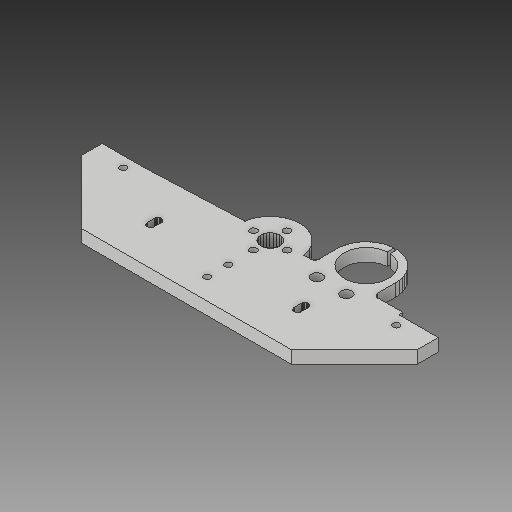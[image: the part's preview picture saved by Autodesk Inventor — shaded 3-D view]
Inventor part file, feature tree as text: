
AUTODESK INVENTOR PART (.ipt)
format: ipt  version: 2017 (Build 210142000, 142)  size: 586,240 bytes
history: native  units: mm
features: sketch x5, reference x4, extrude x3, other x3, hole x2
ambient origin geometry x8: Origin, YZ Plane, XZ Plane, XY Plane, X Axis, Y Axis, Z Axis, Center Point
bodies: Solid1 (feature_tree)
feature tree (17):
  extrude  "Extrusion1"  Depth=6.0mm TaperAngle=0.0deg
  hole  "Hole1"  [1 undecoded]
  hole  "Hole2"  [1 undecoded]
  extrude  "Extrusion2"  [1 undecoded]
  extrude  "Extrusion3"  [1 undecoded]
  sketch  "Sketch1"  dims[d0=6.0mm d1=0.0mm]
  sketch  "Sketch2"  dims[d2=3.2mm d3=6.0mm d4=4.0mm d5=2.0mm d6=90.0deg d7=8.0mm d8=20.594885mm]
  sketch  "Sketch3"  dims[d9=21.2mm d10=6.0mm d11=4.0mm d12=2.0mm d13=90.0deg d14=8.0mm d15=20.594885mm d16=6.0mm d17=0.0mm]
  sketch  "Sketch4"  dims[d18=6.0mm d19=0.0mm]
  sketch  "Sketch5"
  reference  "Reference1"
  reference  "Reference2"
  reference  "Reference3"
  reference  "Reference4"
  other  "<userpath>\OneDrive\Inventor\Beast 3D Printer\Rear-Bed-Holder.iam"
  other  "Rear-Bed-Holder.iam"
  other  "Rear-Bed-Holder-mid:1"
note: 4 required parameter values undecoded (feature->parameter linkage not recoverable at this tier; creation-order binding heuristic only, values carry confidence <= 0.55)
